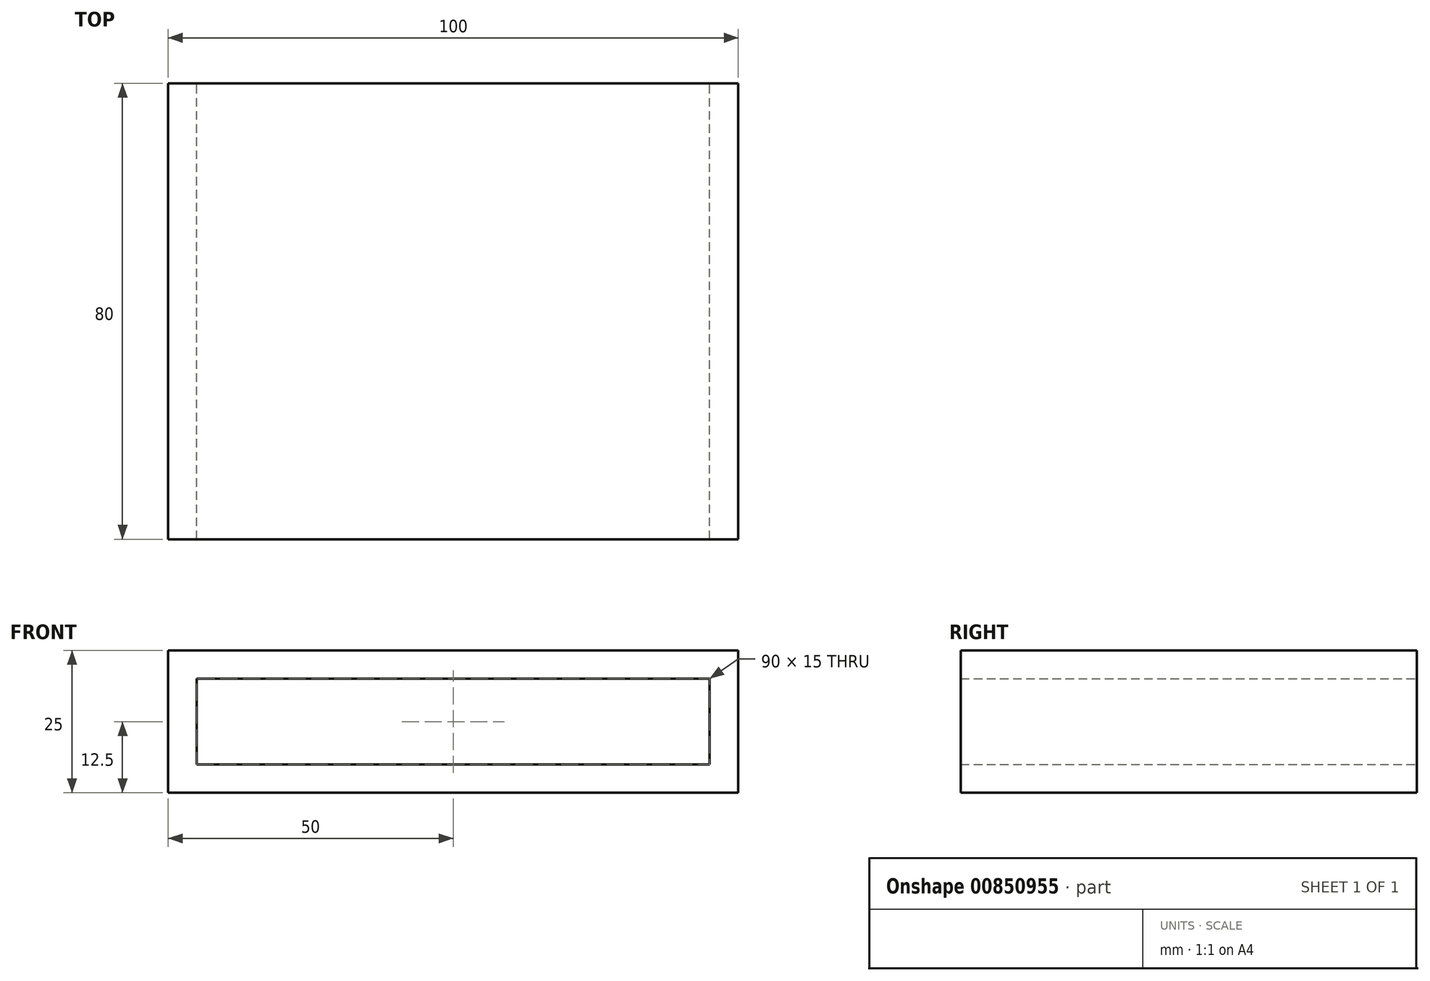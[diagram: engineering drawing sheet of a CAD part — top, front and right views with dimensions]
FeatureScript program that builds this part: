
annotation { "Feature Type Name" : "Feature", "Feature Type Description" : "" }
export const myFeature = defineFeature(function(context is Context, id is Id, definition is map)
    precondition{}
    {
        {
            assignVariable(context, id + "F0", {"name" : "shelf_depth", "anyValue" : 80});
        }
        {
            var Q0;
            Q0=qCreatedBy(makeId("Front.planeOp"),FACE);
            var sketch = newSketch(context, id + "F1", { "sketchPlane" : qUnion([Q0])});
            skPoint(sketch, "E0.middle", {"position": v(0, 0) * mm});
            skLineSegment(sketch, "E1", {"start": v(0, 12.5) * mm, "end": v(50, 12.5) * mm});
            skLineSegment(sketch, "E2", {"start": v(50, -12.5) * mm, "end": v(0, -12.5) * mm});
            skLineSegment(sketch, "E3", {"start": v(0, -12.5) * mm, "end": v(0, -7.5) * mm});
            skLineSegment(sketch, "E4", {"start": v(0, -7.5) * mm, "end": v(45, -7.5) * mm});
            skLineSegment(sketch, "E5", {"start": v(45, -7.5) * mm, "end": v(45, 7.5) * mm});
            skLineSegment(sketch, "E6", {"start": v(45, 7.5) * mm, "end": v(0, 7.5) * mm});
            skLineSegment(sketch, "E7", {"start": v(0, 7.5) * mm, "end": v(0, 12.5) * mm});
            skLineSegment(sketch, "E8", {"start": v(50, 12.5) * mm, "end": v(50, -12.5) * mm});
            skSolve(sketch);
        }
        {
            var Q0;
            Q0 = qSketchRegion(id + "F1", true);
            extrude(context, id + "F2", {"entities" : qUnion([Q0]), "depth" : (getVariable(context, 'shelf_depth')) * mm, "offsetDistance" : 25 * mm});
        }
        {
            var Q0;
            Q0=makeQuery(id+"F2.opExtrude","SWEPT_BODY",BODY,{"disambiguationData":[OSD([sQuery(id+"F1.wireOp",EDGE,"E1"),sQuery(id+"F1.wireOp",EDGE,"E2"),sQuery(id+"F1.wireOp",EDGE,"E3"),sQuery(id+"F1.wireOp",EDGE,"E4"),sQuery(id+"F1.wireOp",EDGE,"E5"),sQuery(id+"F1.wireOp",EDGE,"E6"),sQuery(id+"F1.wireOp",EDGE,"E7"),sQuery(id+"F1.wireOp",EDGE,"E8")])]});
            var Q1;
            Q1=qCreatedBy(makeId("Right.planeOp"),FACE);
            mirror(context, id + "F3", {"operationType" : NewBodyOperationType.ADD, "entities" : qUnion([Q0]), "mirrorPlane" : qUnion([Q1])});
        }
    });
